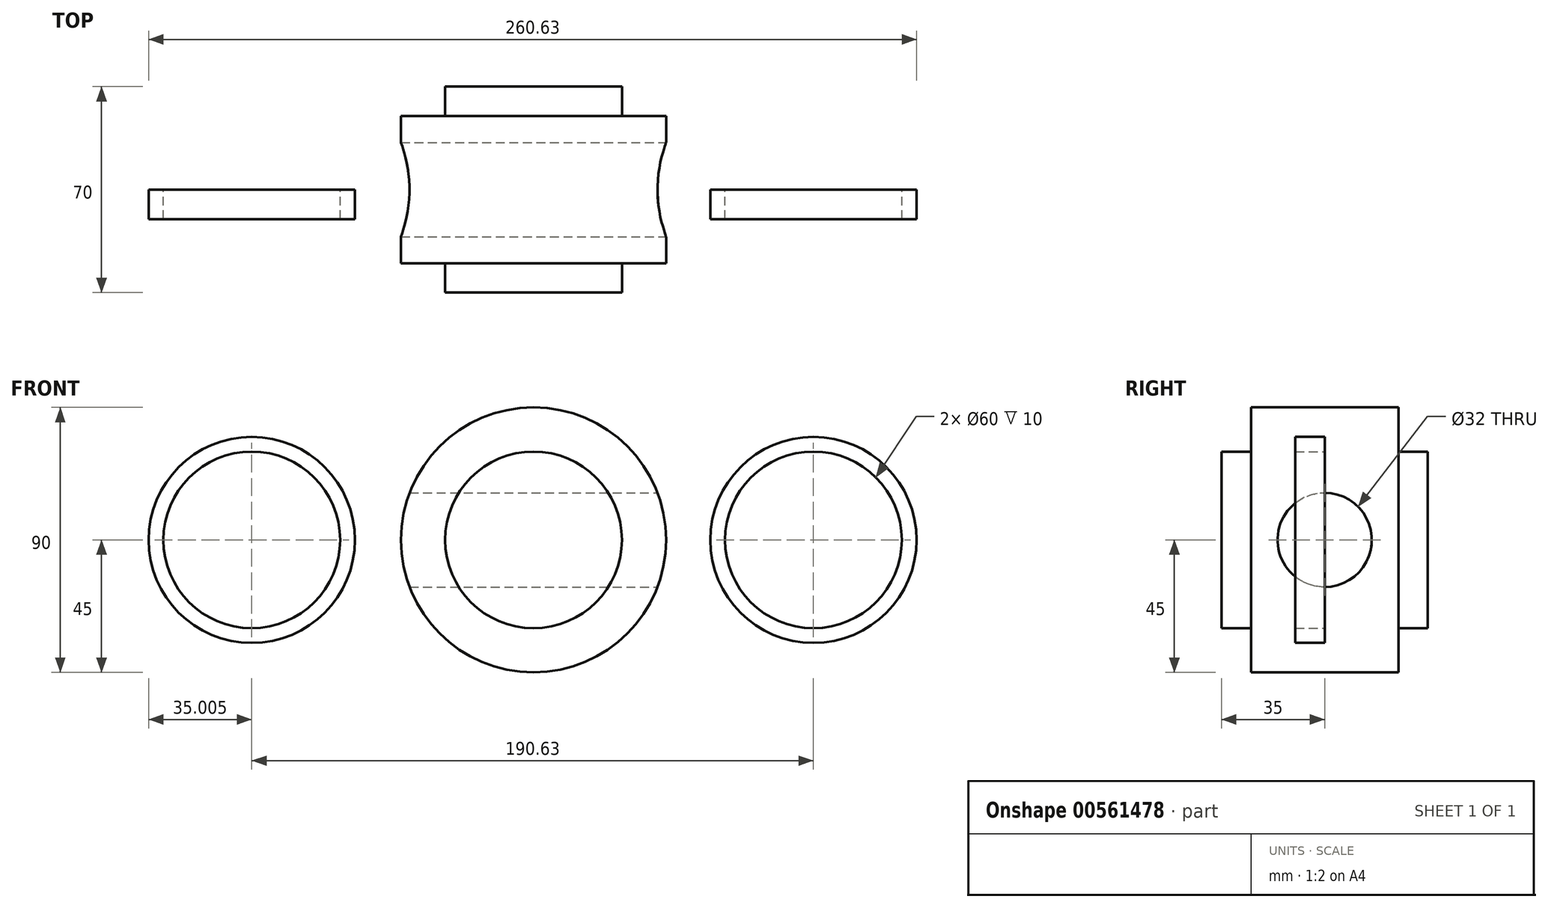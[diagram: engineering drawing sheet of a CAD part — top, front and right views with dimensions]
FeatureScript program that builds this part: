
annotation { "Feature Type Name" : "Feature", "Feature Type Description" : "" }
export const myFeature = defineFeature(function(context is Context, id is Id, definition is map)
    precondition{}
    {
        {
            var Q0;
            Q0=qCreatedBy(makeId("Front.planeOp"),FACE);
            var sketch = newSketch(context, id + "F0", { "sketchPlane" : qUnion([Q0])});
            skCircle(sketch, "E0", {"center": v(0, 0) * mm, "radius": 30 * mm});
            skCircle(sketch, "E1", {"center": v(0, 0) * mm, "radius": 45 * mm});
            skSolve(sketch);
        }
        {
            var Q0;
            Q0=makeQuery(id+"F0.imprint","IMPRINT",FACE,{"disambiguationData":[TD([[makeQuery(id+"F0.imprint","IMPRINT",EDGE,{"derivedFrom":sQuery(id+"F0.wireOp",EDGE,"E0")}),1.0]])]});
            extrude(context, id + "F1", {"entities" : qUnion([Q0]), "endBound" : BoundingType.SYMMETRIC, "depth" : 70 * mm, "offsetDistance" : 25 * mm});
        }
        {
            var Q0;
            Q0 = qSketchRegion(id + "F0", true);
            extrude(context, id + "F2", {"entities" : qUnion([Q0]), "operationType" : NewBodyOperationType.ADD, "endBound" : BoundingType.SYMMETRIC, "depth" : 50 * mm, "offsetDistance" : 25 * mm});
        }
        {
            var Q0;
            Q0=qCreatedBy(makeId("Right.planeOp"),FACE);
            var sketch = newSketch(context, id + "F3", { "sketchPlane" : qUnion([Q0])});
            skCircle(sketch, "E2", {"center": v(0, 0) * mm, "radius": 16 * mm});
            skSolve(sketch);
        }
        {
            var Q0;
            Q0 = qSketchRegion(id + "F3", true);
            extrude(context, id + "F4", {"entities" : qUnion([Q0]), "operationType" : NewBodyOperationType.REMOVE, "endBound" : BoundingType.SYMMETRIC, "oppositeDirection" : true, "depth" : 90 * mm, "offsetDistance" : 25 * mm});
        }
        {
            var Q0;
            Q0=qCreatedBy(makeId("Front.planeOp"),FACE);
            var sketch = newSketch(context, id + "F5", { "sketchPlane" : qUnion([Q0])});
            skCircle(sketch, "E3", {"center": v(95, 0) * mm, "radius": 30 * mm});
            skCircle(sketch, "E4", {"center": v(95, 0) * mm, "radius": 35 * mm});
            skCircle(sketch, "E5", {"center": v(-95.63, 0) * mm, "radius": 35 * mm});
            skCircle(sketch, "E6", {"center": v(-95.63, 0) * mm, "radius": 30 * mm});
            skSolve(sketch);
        }
        {
            var Q0;
            Q0 = qSketchRegion(id + "F5", true);
            extrude(context, id + "F6", {"entities" : qUnion([Q0]), "depth" : 10 * mm, "offsetDistance" : 25 * mm});
        }
    });
